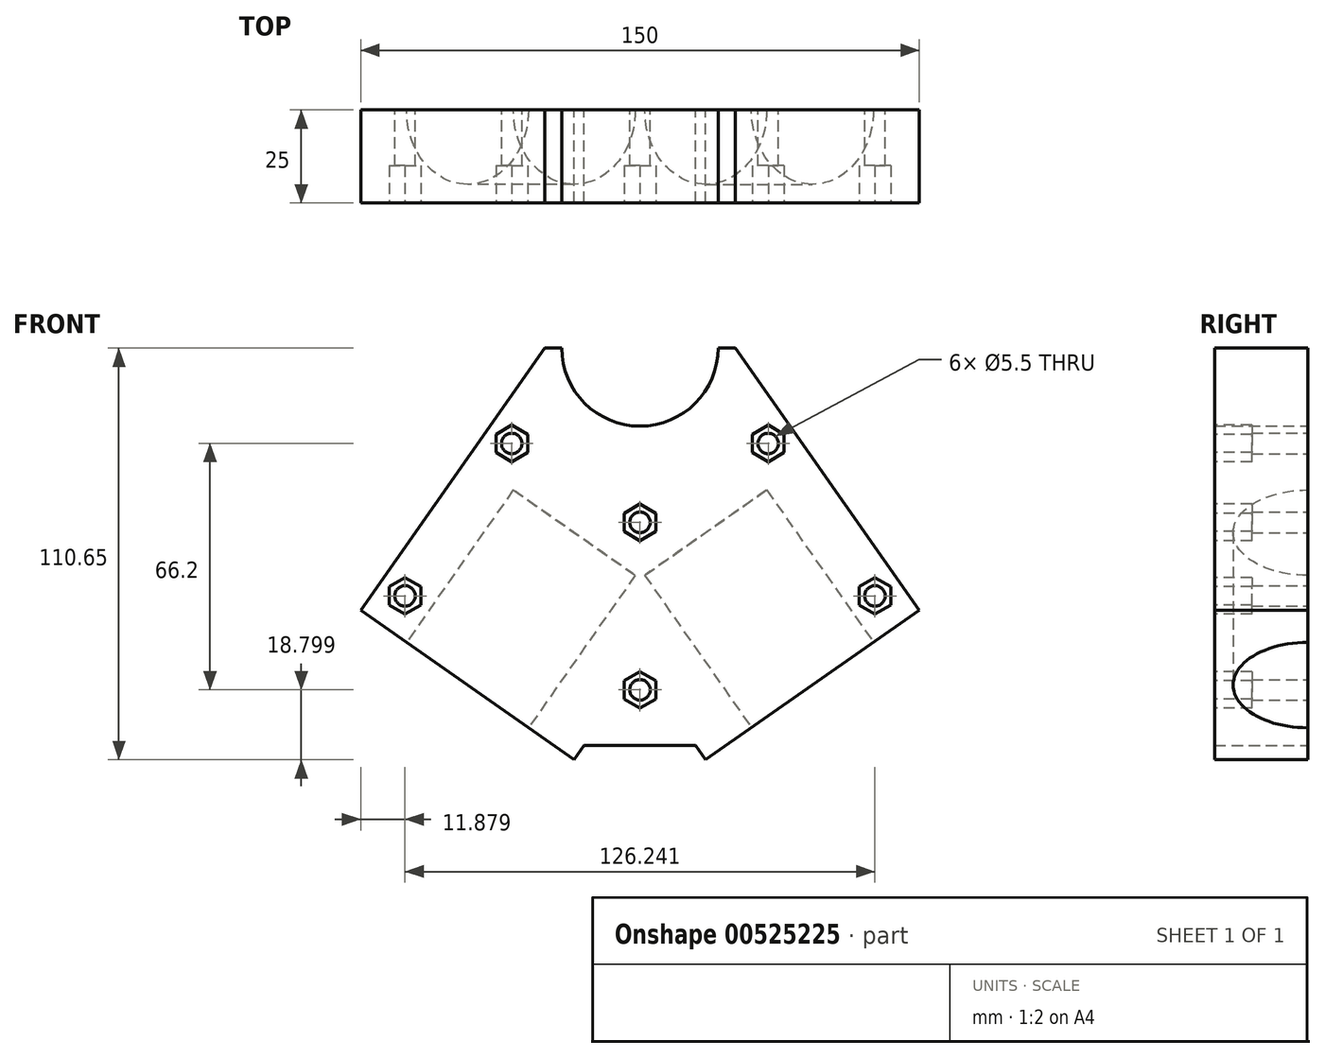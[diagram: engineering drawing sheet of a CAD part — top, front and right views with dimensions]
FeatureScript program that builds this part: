
annotation { "Feature Type Name" : "Feature", "Feature Type Description" : "" }
export const myFeature = defineFeature(function(context is Context, id is Id, definition is map)
    precondition{}
    {
        {
            var Q0;
            Q0=qCreatedBy(makeId("Front.planeOp"),FACE);
            var sketch = newSketch(context, id + "F0", { "sketchPlane" : qUnion([Q0])});
            skArc(sketch, "E0", {"start": v(21, 0) * mm, "mid": v(0, -21) * mm, "end": v(-21, 0) * mm});
            skLineSegment(sketch, "E1", {"start": v(-21, 0) * mm, "end": v(-25.64, 0) * mm});
            skLineSegment(sketch, "E2", {"start": v(-25.64, 0) * mm, "end": v(-75, -70.5) * mm});
            skLineSegment(sketch, "E3", {"start": v(-75, -70.5) * mm, "end": v(-17.66, -110.65) * mm});
            skLineSegment(sketch, "E4", {"start": v(-17.66, -110.65) * mm, "end": v(-15, -106.85) * mm});
            skLineSegment(sketch, "E5", {"start": v(-15, -106.85) * mm, "end": v(15, -106.85) * mm});
            skLineSegment(sketch, "E6", {"start": v(15, -106.85) * mm, "end": v(17.66, -110.65) * mm});
            skLineSegment(sketch, "E7", {"start": v(17.66, -110.65) * mm, "end": v(75, -70.5) * mm});
            skLineSegment(sketch, "E8", {"start": v(75, -70.5) * mm, "end": v(25.64, 0) * mm});
            skLineSegment(sketch, "E9", {"start": v(25.64, 0) * mm, "end": v(21, 0) * mm});
            skSolve(sketch);
        }
        {
            var Q0;
            Q0 = qSketchRegion(id + "F0", true);
            extrude(context, id + "F1", {"entities" : qUnion([Q0]), "depth" : 25 * mm, "offsetDistance" : 25 * mm});
        }
        {
            var Q0;
            Q0=makeQuery(id+"F1.opExtrude","SWEPT_FACE",FACE,{"disambiguationData":[OSD([sQuery(id+"F0.wireOp",EDGE,"E3")])]});
            var sketch = newSketch(context, id + "F2", { "sketchPlane" : qUnion([Q0])});
            skArc(sketch, "E10", {"start": v(-6, 0) * mm, "mid": v(14, 20) * mm, "end": v(34, 0) * mm});
            skLineSegment(sketch, "E11", {"start": v(-6, 0) * mm, "end": v(34, 0) * mm});
            skSolve(sketch);
        }
        {
            var Q0;
            Q0 = qSketchRegion(id + "F2", true);
            extrude(context, id + "F3", {"entities" : qUnion([Q0]), "operationType" : NewBodyOperationType.REMOVE, "oppositeDirection" : true, "depth" : 50 * mm, "offsetDistance" : 25 * mm});
        }
        {
            var Q0;
            Q0=makeQuery(id+"F1.opExtrude","SWEPT_FACE",FACE,{"disambiguationData":[OSD([sQuery(id+"F0.wireOp",EDGE,"E7")])]});
            var sketch = newSketch(context, id + "F4", { "sketchPlane" : qUnion([Q0])});
            skArc(sketch, "E12", {"start": v(-34, 0) * mm, "mid": v(-14, 20) * mm, "end": v(6, 0) * mm});
            skLineSegment(sketch, "E13", {"start": v(6, 0) * mm, "end": v(-34, 0) * mm});
            skSolve(sketch);
        }
        {
            var Q0;
            Q0 = qSketchRegion(id + "F4", true);
            extrude(context, id + "F5", {"entities" : qUnion([Q0]), "operationType" : NewBodyOperationType.REMOVE, "oppositeDirection" : true, "depth" : 50 * mm, "offsetDistance" : 25 * mm});
        }
        {
            var Q0;
            Q0=makeQuery(id+"F1.opExtrude","CAP_FACE",FACE,{"disambiguationData":[OSD([sQuery(id+"F0.wireOp",EDGE,"E0"),sQuery(id+"F0.wireOp",EDGE,"E1"),sQuery(id+"F0.wireOp",EDGE,"E2"),sQuery(id+"F0.wireOp",EDGE,"E3"),sQuery(id+"F0.wireOp",EDGE,"E4"),sQuery(id+"F0.wireOp",EDGE,"E5"),sQuery(id+"F0.wireOp",EDGE,"E6"),sQuery(id+"F0.wireOp",EDGE,"E7"),sQuery(id+"F0.wireOp",EDGE,"E8"),sQuery(id+"F0.wireOp",EDGE,"E9")])],"isStart":true});
            var sketch = newSketch(context, id + "F6", { "sketchPlane" : qUnion([Q0])});
            skCircle(sketch, "E14", {"center": v(-63.12, -66.6) * mm, "radius": 2.75 * mm});
            skCircle(sketch, "E15", {"center": v(-34.44, -25.65) * mm, "radius": 2.75 * mm});
            skCircle(sketch, "E16", {"center": v(34.44, -25.65) * mm, "radius": 2.75 * mm});
            skCircle(sketch, "E17", {"center": v(63.12, -66.6) * mm, "radius": 2.75 * mm});
            skCircle(sketch, "E18", {"center": v(0, -46.85) * mm, "radius": 2.75 * mm});
            skCircle(sketch, "E19", {"center": v(0, -91.85) * mm, "radius": 2.75 * mm});
            skLineSegment(sketch, "E20", {"start": v(0, -46.85) * mm, "end": v(0, -91.85) * mm});
            skLineSegment(sketch, "E21", {"start": v(-63.12, -66.6) * mm, "end": v(-34.44, -25.65) * mm});
            skLineSegment(sketch, "E22", {"start": v(34.44, -25.65) * mm, "end": v(63.12, -66.6) * mm});
            skSolve(sketch);
        }
        {
            var Q0;
            Q0=makeQuery(id+"F6.imprint","IMPRINT",FACE,{"disambiguationData":[TD([[makeQuery(id+"F6.imprint","IMPRINT",EDGE,{"derivedFrom":sQuery(id+"F6.wireOp",EDGE,"E14")}),1.0]])]});
            var Q1;
            Q1=makeQuery(id+"F6.imprint","IMPRINT",FACE,{"disambiguationData":[TD([[makeQuery(id+"F6.imprint","IMPRINT",EDGE,{"derivedFrom":sQuery(id+"F6.wireOp",EDGE,"E16")}),1.0]])]});
            var Q2;
            Q2=makeQuery(id+"F6.imprint","IMPRINT",FACE,{"disambiguationData":[TD([[makeQuery(id+"F6.imprint","IMPRINT",EDGE,{"derivedFrom":sQuery(id+"F6.wireOp",EDGE,"E17")}),1.0]])]});
            var Q3;
            Q3=makeQuery(id+"F6.imprint","IMPRINT",FACE,{"disambiguationData":[TD([[makeQuery(id+"F6.imprint","IMPRINT",EDGE,{"derivedFrom":sQuery(id+"F6.wireOp",EDGE,"E18")}),1.0]])]});
            var Q4;
            Q4=makeQuery(id+"F6.imprint","IMPRINT",FACE,{"disambiguationData":[TD([[makeQuery(id+"F6.imprint","IMPRINT",EDGE,{"derivedFrom":sQuery(id+"F6.wireOp",EDGE,"E19")}),1.0]])]});
            var Q5;
            Q5=makeQuery(id+"F6.imprint","IMPRINT",FACE,{"disambiguationData":[TD([[makeQuery(id+"F6.imprint","IMPRINT",EDGE,{"derivedFrom":sQuery(id+"F6.wireOp",EDGE,"E15")}),1.0]])]});
            extrude(context, id + "F7", {"entities" : qUnion([Q0, Q1, Q2, Q3, Q4, Q5]), "operationType" : NewBodyOperationType.REMOVE, "endBound" : BoundingType.THROUGH_ALL, "oppositeDirection" : true, "depth" : 25 * mm, "offsetDistance" : 25 * mm});
        }
        {
            var Q0;
            Q0=makeQuery(id+"F1.opExtrude","CAP_FACE",FACE,{"disambiguationData":[OSD([sQuery(id+"F0.wireOp",EDGE,"E0"),sQuery(id+"F0.wireOp",EDGE,"E1"),sQuery(id+"F0.wireOp",EDGE,"E2"),sQuery(id+"F0.wireOp",EDGE,"E3"),sQuery(id+"F0.wireOp",EDGE,"E4"),sQuery(id+"F0.wireOp",EDGE,"E5"),sQuery(id+"F0.wireOp",EDGE,"E6"),sQuery(id+"F0.wireOp",EDGE,"E7"),sQuery(id+"F0.wireOp",EDGE,"E8"),sQuery(id+"F0.wireOp",EDGE,"E9")])],"isStart":false});
            var sketch = newSketch(context, id + "F8", { "sketchPlane" : qUnion([Q0])});
            skCircle(sketch, "E23.cCircle", {"center": v(-34.44, -25.65) * mm, "radius": 4.25 * mm, "construction": true});
            skLineSegment(sketch, "E23.0", {"start": v(-30.2, -23.2) * mm, "end": v(-30.2, -28.1) * mm});
            skLineSegment(sketch, "E23.1", {"start": v(-30.2, -28.1) * mm, "end": v(-34.44, -30.56) * mm});
            skLineSegment(sketch, "E23.2", {"start": v(-34.44, -30.56) * mm, "end": v(-38.7, -28.1) * mm});
            skLineSegment(sketch, "E23.3", {"start": v(-38.7, -28.1) * mm, "end": v(-38.7, -23.2) * mm});
            skLineSegment(sketch, "E23.4", {"start": v(-38.7, -23.2) * mm, "end": v(-34.44, -20.74) * mm});
            skLineSegment(sketch, "E23.5", {"start": v(-34.44, -20.74) * mm, "end": v(-30.2, -23.2) * mm});
            skPoint(sketch, "E23.0.midPoint", {"position": v(-30.2, -25.65) * mm});
            skCircle(sketch, "E24.cCircle", {"center": v(-63.12, -66.6) * mm, "radius": 4.25 * mm, "construction": true});
            skLineSegment(sketch, "E24.0", {"start": v(-58.87, -64.16) * mm, "end": v(-58.87, -69.06) * mm});
            skLineSegment(sketch, "E24.1", {"start": v(-58.87, -69.06) * mm, "end": v(-63.12, -71.52) * mm});
            skLineSegment(sketch, "E24.2", {"start": v(-63.12, -71.52) * mm, "end": v(-67.37, -69.06) * mm});
            skLineSegment(sketch, "E24.3", {"start": v(-67.37, -69.06) * mm, "end": v(-67.37, -64.16) * mm});
            skLineSegment(sketch, "E24.4", {"start": v(-67.37, -64.16) * mm, "end": v(-63.12, -61.7) * mm});
            skLineSegment(sketch, "E24.5", {"start": v(-63.12, -61.7) * mm, "end": v(-58.87, -64.16) * mm});
            skPoint(sketch, "E24.0.midPoint", {"position": v(-58.87, -66.6) * mm});
            skCircle(sketch, "E25.cCircle", {"center": v(0, -91.85) * mm, "radius": 4.25 * mm, "construction": true});
            skLineSegment(sketch, "E25.0", {"start": v(4.25, -89.4) * mm, "end": v(4.25, -94.3) * mm});
            skLineSegment(sketch, "E25.1", {"start": v(4.25, -94.3) * mm, "end": v(0, -96.76) * mm});
            skLineSegment(sketch, "E25.2", {"start": v(0, -96.76) * mm, "end": v(-4.25, -94.3) * mm});
            skLineSegment(sketch, "E25.3", {"start": v(-4.25, -94.3) * mm, "end": v(-4.25, -89.4) * mm});
            skLineSegment(sketch, "E25.4", {"start": v(-4.25, -89.4) * mm, "end": v(0, -86.94) * mm});
            skLineSegment(sketch, "E25.5", {"start": v(0, -86.94) * mm, "end": v(4.25, -89.4) * mm});
            skPoint(sketch, "E25.0.midPoint", {"position": v(4.25, -91.85) * mm});
            skCircle(sketch, "E26.cCircle", {"center": v(0, -46.85) * mm, "radius": 4.25 * mm, "construction": true});
            skLineSegment(sketch, "E26.0", {"start": v(4.25, -44.4) * mm, "end": v(4.25, -49.3) * mm});
            skLineSegment(sketch, "E26.1", {"start": v(4.25, -49.3) * mm, "end": v(0, -51.76) * mm});
            skLineSegment(sketch, "E26.2", {"start": v(0, -51.76) * mm, "end": v(-4.25, -49.3) * mm});
            skLineSegment(sketch, "E26.3", {"start": v(-4.25, -49.3) * mm, "end": v(-4.25, -44.4) * mm});
            skLineSegment(sketch, "E26.4", {"start": v(-4.25, -44.4) * mm, "end": v(0, -41.94) * mm});
            skLineSegment(sketch, "E26.5", {"start": v(0, -41.94) * mm, "end": v(4.25, -44.4) * mm});
            skPoint(sketch, "E26.0.midPoint", {"position": v(4.25, -46.85) * mm});
            skCircle(sketch, "E27.cCircle", {"center": v(34.44, -25.65) * mm, "radius": 4.25 * mm, "construction": true});
            skLineSegment(sketch, "E27.0", {"start": v(30.2, -28.1) * mm, "end": v(30.2, -23.2) * mm});
            skLineSegment(sketch, "E27.1", {"start": v(30.2, -23.2) * mm, "end": v(34.44, -20.74) * mm});
            skLineSegment(sketch, "E27.2", {"start": v(34.44, -20.74) * mm, "end": v(38.7, -23.2) * mm});
            skLineSegment(sketch, "E27.3", {"start": v(38.7, -23.2) * mm, "end": v(38.7, -28.1) * mm});
            skLineSegment(sketch, "E27.4", {"start": v(38.7, -28.1) * mm, "end": v(34.44, -30.56) * mm});
            skLineSegment(sketch, "E27.5", {"start": v(34.44, -30.56) * mm, "end": v(30.2, -28.1) * mm});
            skPoint(sketch, "E27.0.midPoint", {"position": v(30.2, -25.65) * mm});
            skCircle(sketch, "E28.cCircle", {"center": v(63.12, -66.6) * mm, "radius": 4.25 * mm, "construction": true});
            skLineSegment(sketch, "E28.0", {"start": v(58.87, -69.06) * mm, "end": v(58.87, -64.16) * mm});
            skLineSegment(sketch, "E28.1", {"start": v(58.87, -64.16) * mm, "end": v(63.12, -61.7) * mm});
            skLineSegment(sketch, "E28.2", {"start": v(63.12, -61.7) * mm, "end": v(67.37, -64.16) * mm});
            skLineSegment(sketch, "E28.3", {"start": v(67.37, -64.16) * mm, "end": v(67.37, -69.06) * mm});
            skLineSegment(sketch, "E28.4", {"start": v(67.37, -69.06) * mm, "end": v(63.12, -71.52) * mm});
            skLineSegment(sketch, "E28.5", {"start": v(63.12, -71.52) * mm, "end": v(58.87, -69.06) * mm});
            skPoint(sketch, "E28.0.midPoint", {"position": v(58.87, -66.6) * mm});
            skSolve(sketch);
        }
        {
            var Q0;
            Q0=makeQuery(id+"F8.imprint","IMPRINT",FACE,{"disambiguationData":[TD([[makeQuery(id+"F8.imprint","IMPRINT",EDGE,{"derivedFrom":sQuery(id+"F8.wireOp",EDGE,"E23.0")}),-1.0]])]});
            var Q1;
            Q1=makeQuery(id+"F8.imprint","IMPRINT",FACE,{"disambiguationData":[TD([[makeQuery(id+"F8.imprint","IMPRINT",EDGE,{"derivedFrom":sQuery(id+"F8.wireOp",EDGE,"E24.0")}),-1.0]])]});
            var Q2;
            Q2=makeQuery(id+"F8.imprint","IMPRINT",FACE,{"disambiguationData":[TD([[makeQuery(id+"F8.imprint","IMPRINT",EDGE,{"derivedFrom":sQuery(id+"F8.wireOp",EDGE,"E25.0")}),-1.0]])]});
            var Q3;
            Q3=makeQuery(id+"F8.imprint","IMPRINT",FACE,{"disambiguationData":[TD([[makeQuery(id+"F8.imprint","IMPRINT",EDGE,{"derivedFrom":sQuery(id+"F8.wireOp",EDGE,"E26.0")}),-1.0]])]});
            var Q4;
            Q4=makeQuery(id+"F8.imprint","IMPRINT",FACE,{"disambiguationData":[TD([[makeQuery(id+"F8.imprint","IMPRINT",EDGE,{"derivedFrom":sQuery(id+"F8.wireOp",EDGE,"E27.0")}),-1.0]])]});
            var Q5;
            Q5=makeQuery(id+"F8.imprint","IMPRINT",FACE,{"disambiguationData":[TD([[makeQuery(id+"F8.imprint","IMPRINT",EDGE,{"derivedFrom":sQuery(id+"F8.wireOp",EDGE,"E28.0")}),-1.0]])]});
            extrude(context, id + "F9", {"entities" : qUnion([Q0, Q1, Q2, Q3, Q4, Q5]), "operationType" : NewBodyOperationType.REMOVE, "oppositeDirection" : true, "depth" : 10 * mm, "offsetDistance" : 25 * mm});
        }
    });
